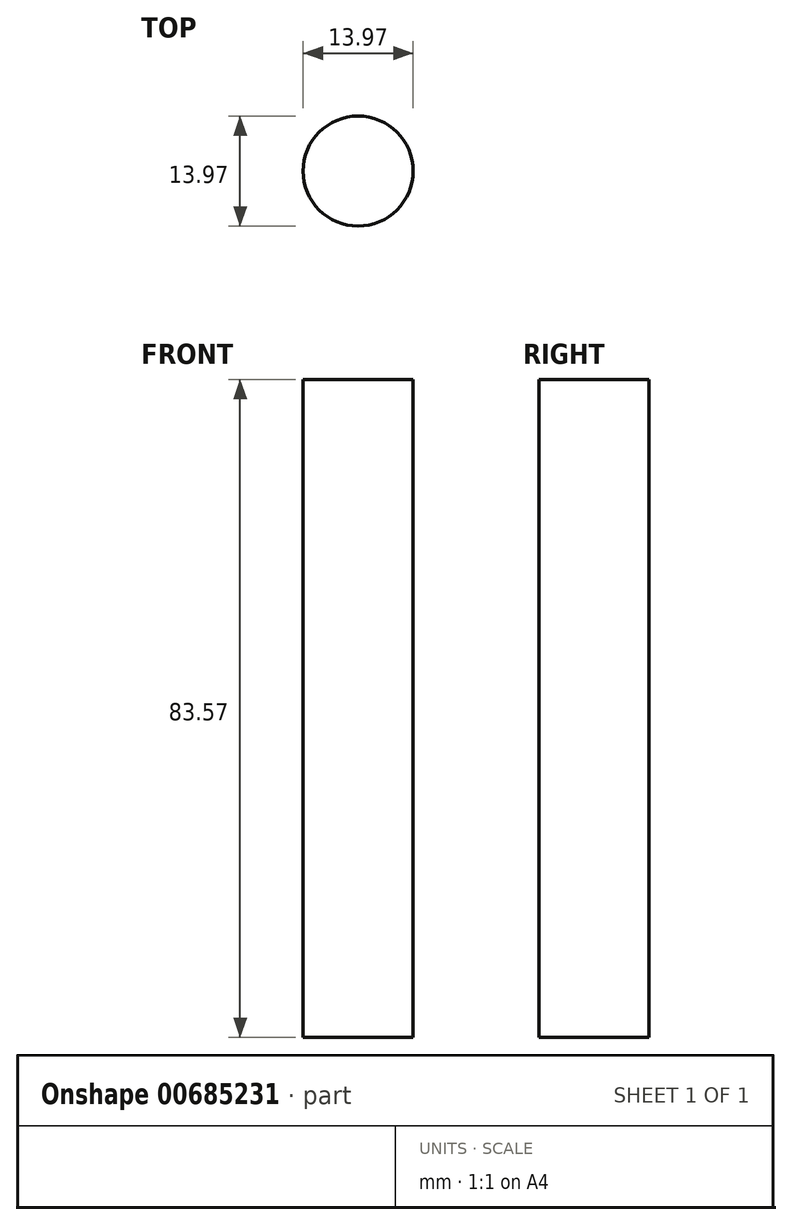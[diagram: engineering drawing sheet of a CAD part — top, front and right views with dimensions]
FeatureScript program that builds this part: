
annotation { "Feature Type Name" : "Feature", "Feature Type Description" : "" }
export const myFeature = defineFeature(function(context is Context, id is Id, definition is map)
    precondition{}
    {
        {
            var Q0;
            Q0=qCreatedBy(makeId("Top.planeOp"),FACE);
            var sketch = newSketch(context, id + "F0", { "sketchPlane" : qUnion([Q0])});
            skCircle(sketch, "E0", {"center": v(-39.5, -6.2) * mm, "radius": 6.99 * mm});
            skSolve(sketch);
        }
        {
            var Q0;
            Q0 = qSketchRegion(id + "F0", true);
            extrude(context, id + "F1", {"entities" : qUnion([Q0]), "depth" : 83.57 * mm, "offsetDistance" : 25.4 * mm});
        }
    });
